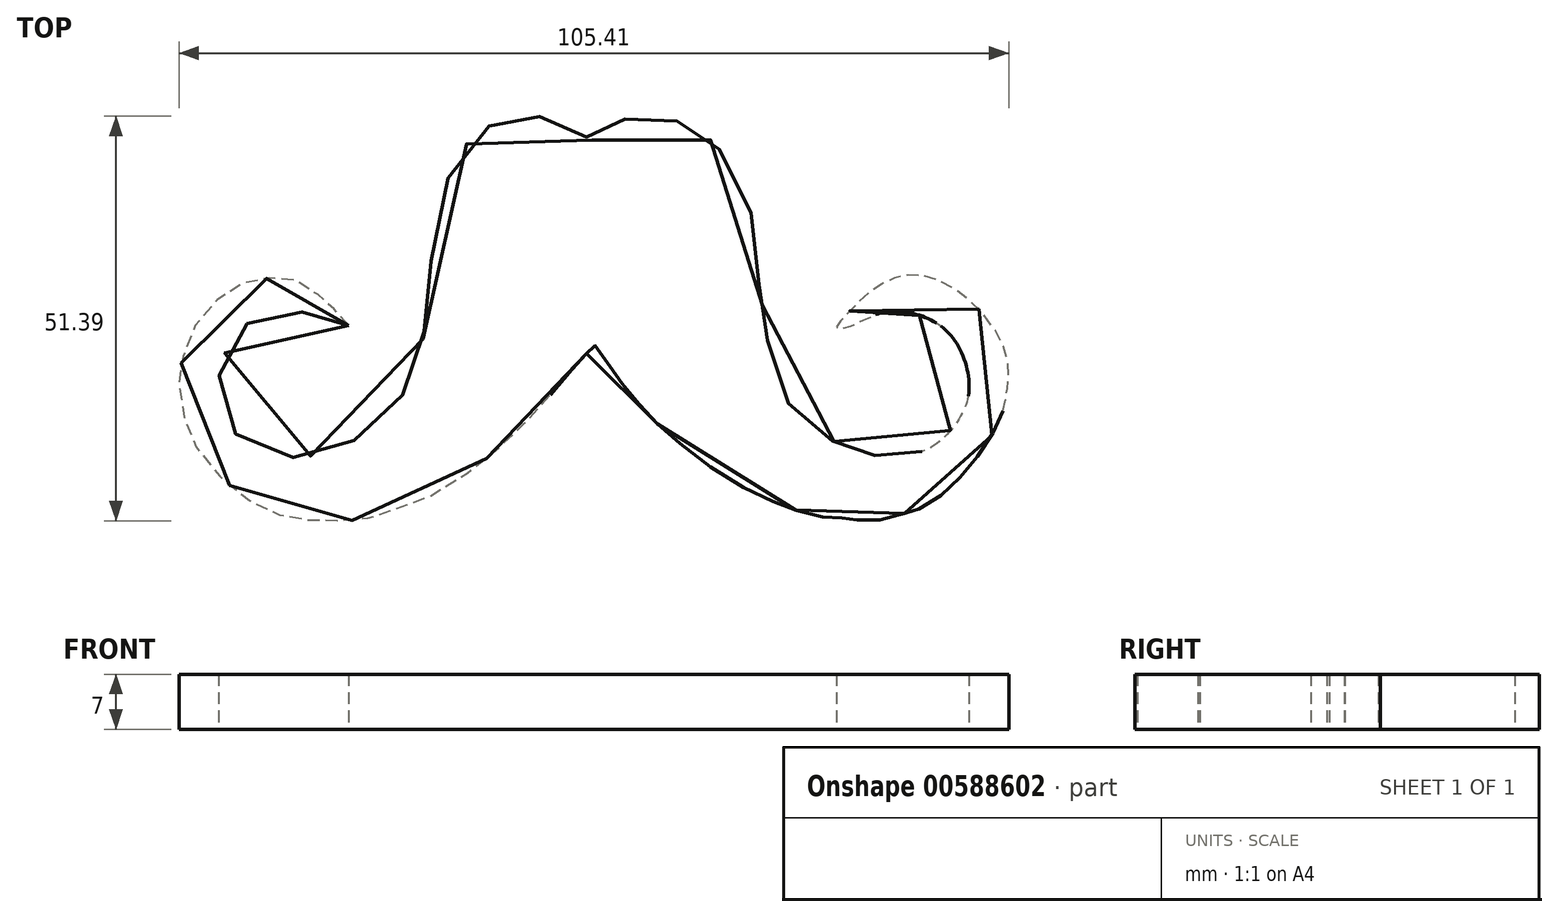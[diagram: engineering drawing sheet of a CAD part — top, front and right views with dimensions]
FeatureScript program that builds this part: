
annotation { "Feature Type Name" : "Feature", "Feature Type Description" : "" }
export const myFeature = defineFeature(function(context is Context, id is Id, definition is map)
    precondition{}
    {
        {
            var Q0;
            Q0=qCreatedBy(makeId("Top.planeOp"),FACE);
            var sketch = newSketch(context, id + "F0", { "sketchPlane" : qUnion([Q0])});
            skPoint(sketch, "E0.25.internal.snap0", {"position": v(-0.2, -21.23) * mm});
            skFitSpline(sketch, "E0", {"points": [v(-31.27, 4.85) * mm, v(-32.47, 6.2) * mm, v(-33.83, 7.86) * mm, v(-35.82, 9.22) * mm, v(-38.53, 10.83) * mm, v(-41.31, 10.9) * mm, v(-44.55, 10.3) * mm, v(-47.7, 8.35) * mm, v(-50.86, 4.67) * mm, v(-52.44, 0.38) * mm, v(-52.8, -2.82) * mm, v(-51.93, -7.57) * mm, v(-49.97, -11.59) * mm, v(-45.38, -16.26) * mm, v(-41, -18.83) * mm, v(-37.08, -19.76) * mm, v(-33.95, -19.85) * mm, v(-29.6, -19.76) * mm, v(-26.82, -18.92) * mm, v(-21.84, -17.23) * mm, v(-14.92, -12.92) * mm, v(-10.32, -8.96) * mm, v(-6.47, -4.9) * mm, v(-2.24, 0) * mm, v(-0.9, 1.58) * mm, v(-0.2, 2.44) * mm, v(1.88, -0.2) * mm, v(3.43, -2.43) * mm, v(6.47, -6.07) * mm, v(9.63, -9.05) * mm, v(16.68, -14.4) * mm, v(23.03, -17.6) * mm, v(26.68, -18.9) * mm, v(30.65, -19.64) * mm, v(31.84, -19.57) * mm, v(33.5, -19.84) * mm, v(36.98, -19.68) * mm, v(40.4, -18.67) * mm, v(40.93, -18.51) * mm, v(44.15, -16.62) * mm, v(47.06, -13.67) * mm, v(50.07, -9.7) * mm, v(51.8, -6.18) * mm, v(52.4, -3.3) * mm, v(52.4, 0.74) * mm, v(48.61, 7.13) * mm, v(42.14, 11.12) * mm, v(37.63, 10.74) * mm, v(33.87, 8.18) * mm, v(31.09, 5.25) * mm, v(30.71, 4.57) * mm, v(31.84, 4.57) * mm, v(35.45, 6.15) * mm, v(38.68, 6.68) * mm, v(43.57, 5.1) * mm, v(46.73, 1.12) * mm, v(47.48, -3.92) * mm, v(45.68, -7.83) * mm, v(41.92, -11) * mm, v(37.33, -11.6) * mm, v(34.7, -11.6) * mm, v(31.39, -10.4) * mm, v(26.88, -7.46) * mm, v(23.04, -2.12) * mm, v(21.61, 5.55) * mm, v(20.86, 10.52) * mm, v(19.73, 19.77) * mm, v(15.75, 27.36) * mm, v(12.14, 30.22) * mm, v(7.7, 31.38) * mm, v(3.08, 30.67) * mm, v(0, 28.37) * mm, v(-3.45, 30.78) * mm, v(-7.96, 31.38) * mm, v(-12.38, 30.67) * mm, v(-17.2, 26.66) * mm, v(-20.51, 15.01) * mm, v(-21.52, 5.88) * mm, v(-23.12, -1.75) * mm, v(-28.24, -8.08) * mm, v(-34.17, -11.29) * mm, v(-41.5, -11.49) * mm, v(-46.61, -7.47) * mm, v(-47.62, -0.95) * mm, v(-44.8, 4.57) * mm, v(-39.49, 6.78) * mm, v(-33.97, 5.68) * mm, v(-31.27, 4.85) * mm]});
            skSolve(sketch);
        }
        {
            var Q0;
            Q0=makeQuery(id+"F0.imprint","IMPRINT",FACE,{"disambiguationData":[TD([[makeQuery(id+"F0.imprint","IMPRINT",EDGE,{"derivedFrom":sQuery(id+"F0.wireOp",EDGE,"E0")}),1.0]])]});
            extrude(context, id + "F1", {"entities" : qUnion([Q0]), "depth" : 7 * mm, "offsetDistance" : 25.4 * mm});
        }
    });
